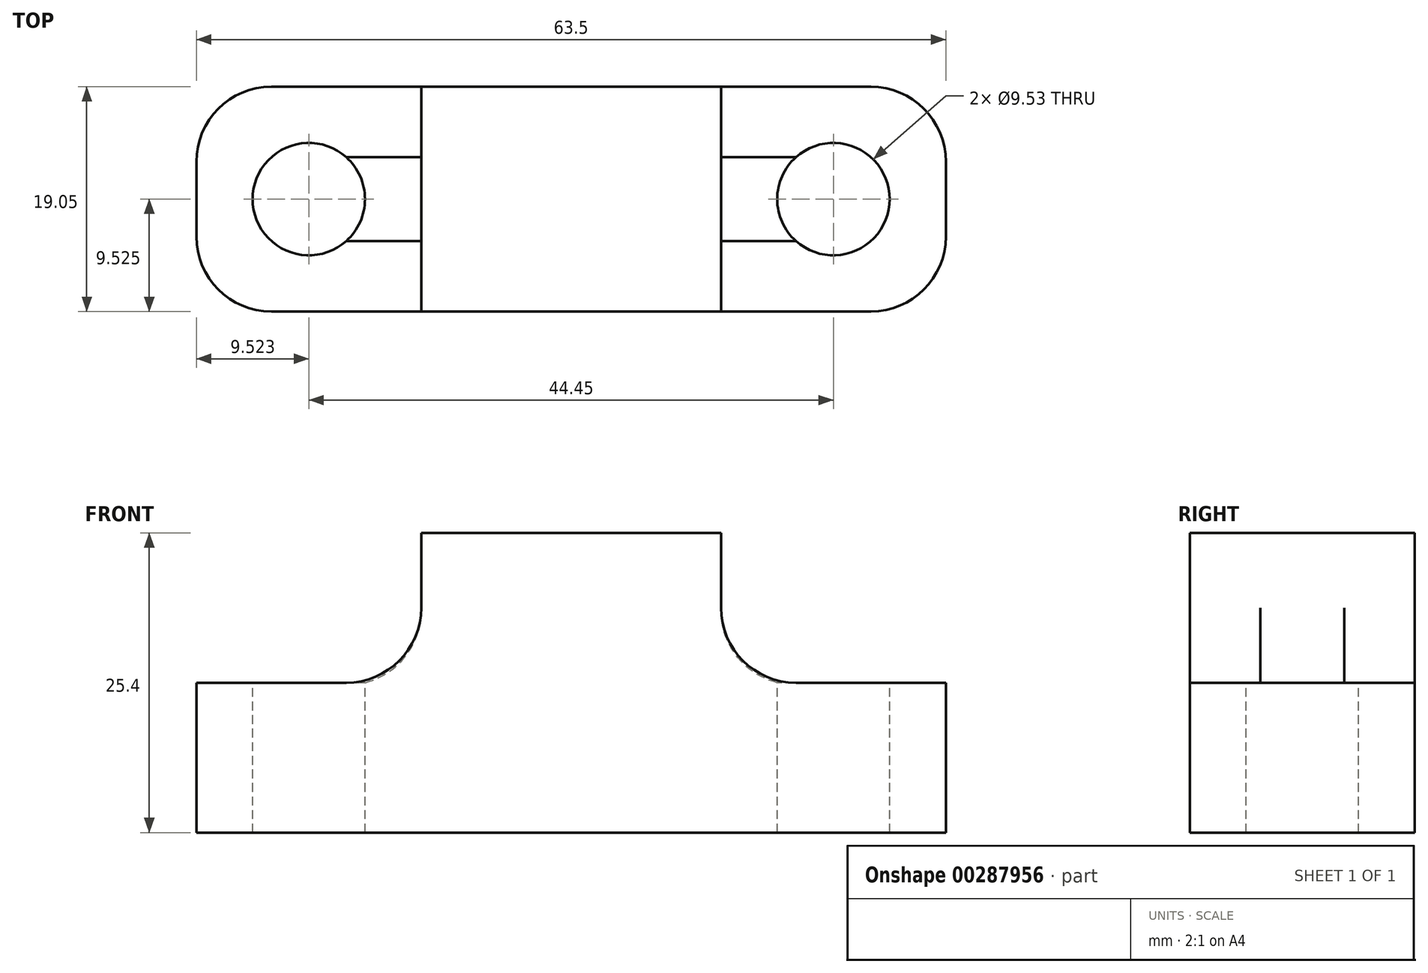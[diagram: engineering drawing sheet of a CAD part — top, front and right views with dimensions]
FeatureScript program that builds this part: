
annotation { "Feature Type Name" : "Feature", "Feature Type Description" : "" }
export const myFeature = defineFeature(function(context is Context, id is Id, definition is map)
    precondition{}
    {
        {
            var Q0;
            Q0=qCreatedBy(makeId("Front.planeOp"),FACE);
            var sketch = newSketch(context, id + "F0", { "sketchPlane" : qUnion([Q0])});
            skLineSegment(sketch, "E0", {"start": v(-35.82, 1.46) * mm, "end": v(-4.07, 1.46) * mm});
            skLineSegment(sketch, "E1", {"start": v(-4.07, 1.46) * mm, "end": v(-4.07, 26.86) * mm});
            skLineSegment(sketch, "E2", {"start": v(-4.07, 26.86) * mm, "end": v(-16.77, 26.86) * mm});
            skLineSegment(sketch, "E3", {"start": v(-16.77, 26.86) * mm, "end": v(-16.77, 14.16) * mm});
            skLineSegment(sketch, "E4", {"start": v(-16.77, 14.16) * mm, "end": v(-35.82, 14.16) * mm});
            skLineSegment(sketch, "E5", {"start": v(-35.82, 14.16) * mm, "end": v(-35.82, 1.46) * mm});
            skSolve(sketch);
        }
        {
            var Q0;
            Q0 = qSketchRegion(id + "F0", true);
            extrude(context, id + "F1", {"entities" : qUnion([Q0]), "depth" : 19.05 * mm});
        }
        {
            var Q0;
            Q0=makeQuery(id+"F1.opExtrude","SWEPT_FACE",FACE,{"disambiguationData":[OSD([sQuery(id+"F0.wireOp",EDGE,"E4")])]});
            var sketch = newSketch(context, id + "F2", { "sketchPlane" : qUnion([Q0])});
            skCircle(sketch, "E6", {"center": v(-26.3, -9.53) * mm, "radius": 4.76 * mm});
            skSolve(sketch);
        }
        {
            var Q0;
            Q0=makeQuery(id+"F2.imprint","IMPRINT",FACE,{"disambiguationData":[TD([[makeQuery(id+"F2.imprint","IMPRINT",EDGE,{"derivedFrom":sQuery(id+"F2.wireOp",EDGE,"E6")}),1.0]])]});
            extrude(context, id + "F3", {"entities" : qUnion([Q0]), "operationType" : NewBodyOperationType.REMOVE, "oppositeDirection" : true, "depth" : 25.4 * mm});
        }
        {
            var Q0;
            Q0=makeQuery(id+"F1.opExtrude","CAP_EDGE",EDGE,{"disambiguationData":[OSD([sQuery(id+"F0.wireOp",EDGE,"E5")])],"isStart":true});
            var Q1;
            Q1=makeQuery(id+"F1.opExtrude","CAP_EDGE",EDGE,{"disambiguationData":[OSD([sQuery(id+"F0.wireOp",EDGE,"E5")])],"isStart":false});
            var Q2;
            Q2=makeQuery(id+"F1.opExtrude","SWEPT_EDGE",EDGE,{"disambiguationData":[OSD([sQuery(id+"F0.wireOp",EDGE,"E3"),sQuery(id+"F0.wireOp",EDGE,"E4")])]});
            fillet(context, id + "F4", {"entities" : qUnion([Q0, Q1, Q2]), "radius" : 6.35 * mm, "tangentPropagation" : true, "allowEdgeOverflow" : false});
        }
        {
            var Q0;
            Q0=makeQuery(id+"F1.opExtrude","SWEPT_BODY",BODY,{"disambiguationData":[OSD([sQuery(id+"F0.wireOp",EDGE,"E0"),sQuery(id+"F0.wireOp",EDGE,"E1"),sQuery(id+"F0.wireOp",EDGE,"E2"),sQuery(id+"F0.wireOp",EDGE,"E3"),sQuery(id+"F0.wireOp",EDGE,"E4"),sQuery(id+"F0.wireOp",EDGE,"E5")])]});
            var Q1;
            Q1=makeQuery(id+"F1.opExtrude","SWEPT_FACE",FACE,{"disambiguationData":[OSD([sQuery(id+"F0.wireOp",EDGE,"E1")])]});
            mirror(context, id + "F5", {"operationType" : NewBodyOperationType.ADD, "entities" : qUnion([Q0]), "mirrorPlane" : qUnion([Q1])});
        }
    });
